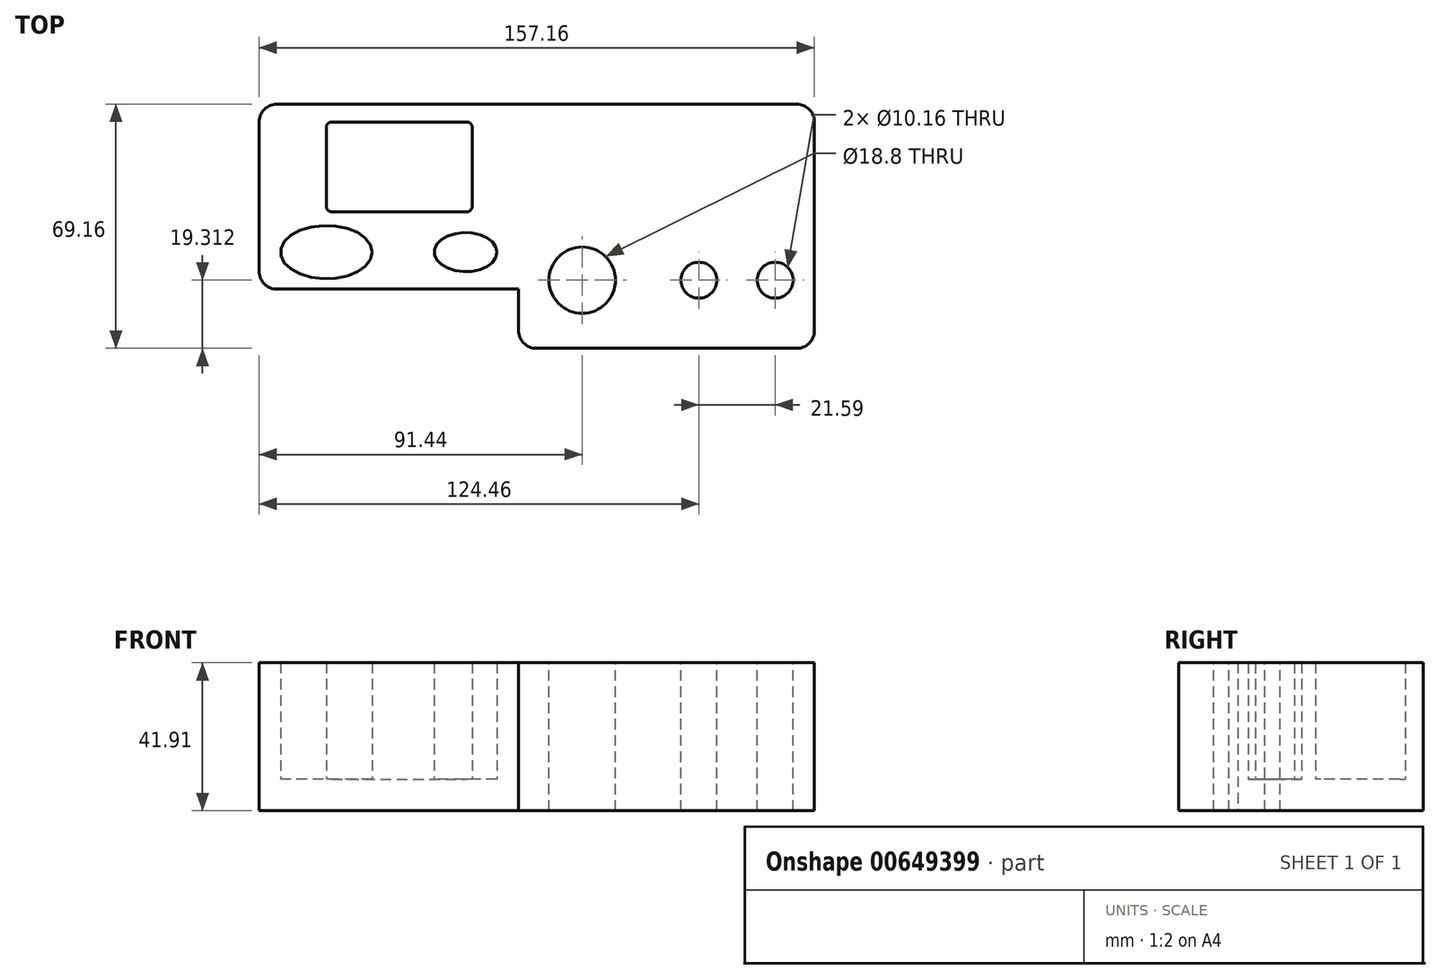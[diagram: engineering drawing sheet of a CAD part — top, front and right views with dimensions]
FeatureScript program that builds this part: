
annotation { "Feature Type Name" : "Feature", "Feature Type Description" : "" }
export const myFeature = defineFeature(function(context is Context, id is Id, definition is map)
    precondition{}
    {
        {
            var Q0;
            Q0=qCreatedBy(makeId("Top.planeOp"),FACE);
            var sketch = newSketch(context, id + "F0", { "sketchPlane" : qUnion([Q0])});
            skLineSegment(sketch, "E0.bottom", {"start": v(0, 0) * mm, "end": v(157.16, 0) * mm});
            skLineSegment(sketch, "E0.top", {"start": v(0, -52.39) * mm, "end": v(157.16, -52.39) * mm});
            skLineSegment(sketch, "E0.left", {"start": v(0, 0) * mm, "end": v(0, -52.39) * mm});
            skLineSegment(sketch, "E0.right", {"start": v(157.16, 0) * mm, "end": v(157.16, -52.39) * mm});
            skLineSegment(sketch, "E1.bottom", {"start": v(19.05, -5.08) * mm, "end": v(60.33, -5.08) * mm});
            skLineSegment(sketch, "E1.top", {"start": v(19.05, -30.48) * mm, "end": v(60.33, -30.48) * mm});
            skLineSegment(sketch, "E1.left", {"start": v(19.05, -5.08) * mm, "end": v(19.05, -30.48) * mm});
            skLineSegment(sketch, "E1.right", {"start": v(60.33, -5.08) * mm, "end": v(60.33, -30.48) * mm});
            skEllipse(sketch, "E2", {"center": v(58.42, -41.9) * mm, "majorRadius": 8.9 * mm, "minorRadius": 5.54 * mm, "majorAxis": v(1, 0)});
            skEllipse(sketch, "E3", {"center": v(19.05, -41.91) * mm, "majorRadius": 12.95 * mm, "minorRadius": 7.56 * mm, "majorAxis": v(1, 0)});
            skSolve(sketch);
        }
        {
            var Q0;
            Q0 = qSketchRegion(id + "F0", true);
            extrude(context, id + "F1", {"entities" : qUnion([Q0]), "depth" : 33.02 * mm, "offsetDistance" : 25.4 * mm});
        }
        {
            var Q0;
            Q0=qCreatedBy(makeId("Top.planeOp"),FACE);
            var sketch = newSketch(context, id + "F2", { "sketchPlane" : qUnion([Q0])});
            skLineSegment(sketch, "E4.bottom", {"start": v(0, 0) * mm, "end": v(73.03, 0) * mm});
            skLineSegment(sketch, "E4.top", {"start": v(0, -52.39) * mm, "end": v(73.03, -52.39) * mm});
            skLineSegment(sketch, "E4.left", {"start": v(0, 0) * mm, "end": v(0, -52.39) * mm});
            skLineSegment(sketch, "E4.right", {"start": v(73.03, 0) * mm, "end": v(73.03, -52.39) * mm});
            skSolve(sketch);
        }
        {
            var Q0;
            Q0 = qSketchRegion(id + "F2", true);
            extrude(context, id + "F3", {"entities" : qUnion([Q0]), "operationType" : NewBodyOperationType.ADD, "oppositeDirection" : true, "depth" : 8.9 * mm, "offsetDistance" : 25.4 * mm});
        }
        {
            var Q0;
            Q0=makeQuery(id+"F3.boolean.opBoolean","MERGE",EDGE,{"derivedFrom":[makeQuery(id+"F1.opExtrude","SWEPT_EDGE",EDGE,{"disambiguationData":[OSD([sQuery(id+"F0.wireOp",EDGE,"E0.top"),sQuery(id+"F0.wireOp",EDGE,"E0.right")])]}),makeQuery(id+"F3.opExtrude","SWEPT_EDGE",EDGE,{"disambiguationData":[OSD([sQuery(id+"F2.wireOp",EDGE,"E4.top"),sQuery(id+"F2.wireOp",EDGE,"E4.right")])]})]});
            var Q1;
            Q1=makeQuery(id+"F3.boolean.opBoolean","MERGE",EDGE,{"derivedFrom":[makeQuery(id+"F1.opExtrude","SWEPT_EDGE",EDGE,{"disambiguationData":[OSD([sQuery(id+"F0.wireOp",EDGE,"E0.bottom"),sQuery(id+"F0.wireOp",EDGE,"E0.right")])]}),makeQuery(id+"F3.opExtrude","SWEPT_EDGE",EDGE,{"disambiguationData":[OSD([sQuery(id+"F2.wireOp",EDGE,"E4.bottom"),sQuery(id+"F2.wireOp",EDGE,"E4.right")])]})]});
            var Q2;
            Q2=makeQuery(id+"F3.boolean.opBoolean","MERGE",EDGE,{"derivedFrom":[makeQuery(id+"F1.opExtrude","SWEPT_EDGE",EDGE,{"disambiguationData":[OSD([sQuery(id+"F0.wireOp",EDGE,"E0.bottom"),sQuery(id+"F0.wireOp",EDGE,"E0.left")])]}),makeQuery(id+"F3.opExtrude","SWEPT_EDGE",EDGE,{"disambiguationData":[OSD([sQuery(id+"F2.wireOp",EDGE,"E4.bottom"),sQuery(id+"F2.wireOp",EDGE,"E4.left")])]})]});
            var Q3;
            Q3=makeQuery(id+"F3.boolean.opBoolean","MERGE",EDGE,{"derivedFrom":[makeQuery(id+"F1.opExtrude","SWEPT_EDGE",EDGE,{"disambiguationData":[OSD([sQuery(id+"F0.wireOp",EDGE,"E0.top"),sQuery(id+"F0.wireOp",EDGE,"E0.left")])]}),makeQuery(id+"F3.opExtrude","SWEPT_EDGE",EDGE,{"disambiguationData":[OSD([sQuery(id+"F2.wireOp",EDGE,"E4.top"),sQuery(id+"F2.wireOp",EDGE,"E4.left")])]})]});
            fillet(context, id + "F4", {"entities" : qUnion([Q0, Q1, Q2, Q3]), "radius" : 5.08 * mm, "tangentPropagation" : true, "allowEdgeOverflow" : false});
        }
        {
            var Q0;
            Q0=makeQuery(id+"F1.opExtrude","SWEPT_EDGE",EDGE,{"disambiguationData":[OSD([sQuery(id+"F0.wireOp",EDGE,"E1.bottom"),sQuery(id+"F0.wireOp",EDGE,"E1.left")])]});
            var Q1;
            Q1=makeQuery(id+"F1.opExtrude","SWEPT_EDGE",EDGE,{"disambiguationData":[OSD([sQuery(id+"F0.wireOp",EDGE,"E1.top"),sQuery(id+"F0.wireOp",EDGE,"E1.left")])]});
            var Q2;
            Q2=makeQuery(id+"F1.opExtrude","SWEPT_EDGE",EDGE,{"disambiguationData":[OSD([sQuery(id+"F0.wireOp",EDGE,"E1.top"),sQuery(id+"F0.wireOp",EDGE,"E1.right")])]});
            var Q3;
            Q3=makeQuery(id+"F1.opExtrude","SWEPT_EDGE",EDGE,{"disambiguationData":[OSD([sQuery(id+"F0.wireOp",EDGE,"E1.bottom"),sQuery(id+"F0.wireOp",EDGE,"E1.right")])]});
            fillet(context, id + "F5", {"entities" : qUnion([Q0, Q1, Q2, Q3]), "radius" : 1.52 * mm, "tangentPropagation" : true, "allowEdgeOverflow" : false});
        }
        {
            var Q0;
            Q0=makeQuery(id+"F8.boolean.opBoolean","MERGE",FACE,{"derivedFrom":[makeQuery(id+"F1.opExtrude","CAP_FACE",FACE,{"disambiguationData":[OSD([sQuery(id+"F0.wireOp",EDGE,"E0.bottom"),sQuery(id+"F0.wireOp",EDGE,"E0.top"),sQuery(id+"F0.wireOp",EDGE,"E0.left"),sQuery(id+"F0.wireOp",EDGE,"E0.right"),sQuery(id+"F0.wireOp",EDGE,"E1.bottom"),sQuery(id+"F0.wireOp",EDGE,"E1.top"),sQuery(id+"F0.wireOp",EDGE,"E1.left"),sQuery(id+"F0.wireOp",EDGE,"E1.right"),sQuery(id+"F0.wireOp",EDGE,"E2"),sQuery(id+"F0.wireOp",EDGE,"E3")])],"isStart":true}),makeQuery(id+"F8.opExtrude","CAP_FACE",FACE,{"disambiguationData":[OSD([sQuery(id+"F7.wireOp",EDGE,"E5.bottom"),sQuery(id+"F7.wireOp",EDGE,"E5.top"),sQuery(id+"F7.wireOp",EDGE,"E5.left"),sQuery(id+"F7.wireOp",EDGE,"E5.right")])],"isStart":true})]});
            extrude(context, id + "F6", {"entities" : qUnion([Q0]), "operationType" : NewBodyOperationType.ADD, "depth" : 8.9 * mm, "offsetDistance" : 25.4 * mm});
        }
        {
            var Q0;
            Q0=qCreatedBy(makeId("Top.planeOp"),FACE);
            var sketch = newSketch(context, id + "F7", { "sketchPlane" : qUnion([Q0])});
            skLineSegment(sketch, "E5.bottom", {"start": v(157.16, 0) * mm, "end": v(73.41, 0) * mm});
            skLineSegment(sketch, "E5.top", {"start": v(157.16, -69.16) * mm, "end": v(73.41, -69.16) * mm});
            skLineSegment(sketch, "E5.left", {"start": v(157.16, 0) * mm, "end": v(157.16, -69.16) * mm});
            skLineSegment(sketch, "E5.right", {"start": v(73.41, 0) * mm, "end": v(73.41, -69.16) * mm});
            skSolve(sketch);
        }
        {
            var Q0;
            Q0=makeQuery(id+"F7.imprint","IMPRINT",FACE,{"disambiguationData":[TD([[makeQuery(id+"F7.imprint","IMPRINT",EDGE,{"derivedFrom":sQuery(id+"F7.wireOp",EDGE,"E5.bottom")}),1.0]])]});
            extrude(context, id + "F8", {"entities" : qUnion([Q0]), "operationType" : NewBodyOperationType.ADD, "depth" : 33.02 * mm, "offsetDistance" : 25.4 * mm});
        }
        {
            var Q0;
            Q0=makeQuery(id+"F8.opExtrude","CAP_FACE",FACE,{"disambiguationData":[OSD([sQuery(id+"F7.wireOp",EDGE,"E5.bottom"),sQuery(id+"F7.wireOp",EDGE,"E5.top"),sQuery(id+"F7.wireOp",EDGE,"E5.left"),sQuery(id+"F7.wireOp",EDGE,"E5.right")])],"isStart":true});
            extrude(context, id + "F9", {"entities" : qUnion([Q0]), "operationType" : NewBodyOperationType.ADD, "depth" : 8.9 * mm, "offsetDistance" : 25.4 * mm});
        }
        {
            var Q0;
            Q0=makeQuery(id+"F1.opExtrude","CAP_FACE",FACE,{"disambiguationData":[OSD([sQuery(id+"F0.wireOp",EDGE,"E0.bottom"),sQuery(id+"F0.wireOp",EDGE,"E0.top"),sQuery(id+"F0.wireOp",EDGE,"E0.left"),sQuery(id+"F0.wireOp",EDGE,"E0.right"),sQuery(id+"F0.wireOp",EDGE,"E1.bottom"),sQuery(id+"F0.wireOp",EDGE,"E1.top"),sQuery(id+"F0.wireOp",EDGE,"E1.left"),sQuery(id+"F0.wireOp",EDGE,"E1.right"),sQuery(id+"F0.wireOp",EDGE,"E2"),sQuery(id+"F0.wireOp",EDGE,"E3")])],"isStart":false});
            var sketch = newSketch(context, id + "F10", { "sketchPlane" : qUnion([Q0])});
            skCircle(sketch, "E6", {"center": v(91.44, -49.85) * mm, "radius": 9.4 * mm});
            skCircle(sketch, "E7", {"center": v(124.46, -49.85) * mm, "radius": 5.08 * mm});
            skCircle(sketch, "E8", {"center": v(146.05, -49.85) * mm, "radius": 5.08 * mm});
            skSolve(sketch);
        }
        {
            var Q0;
            Q0=makeQuery(id+"F10.imprint","IMPRINT",FACE,{"disambiguationData":[TD([[makeQuery(id+"F10.imprint","IMPRINT",EDGE,{"derivedFrom":sQuery(id+"F10.wireOp",EDGE,"E6")}),1.0]])]});
            var Q1;
            Q1=makeQuery(id+"F10.imprint","IMPRINT",FACE,{"disambiguationData":[TD([[makeQuery(id+"F10.imprint","IMPRINT",EDGE,{"derivedFrom":sQuery(id+"F10.wireOp",EDGE,"E7")}),1.0]])]});
            var Q2;
            Q2=makeQuery(id+"F10.imprint","IMPRINT",FACE,{"disambiguationData":[TD([[makeQuery(id+"F10.imprint","IMPRINT",EDGE,{"derivedFrom":sQuery(id+"F10.wireOp",EDGE,"E8")}),1.0]])]});
            extrude(context, id + "F11", {"entities" : qUnion([Q0, Q1, Q2]), "operationType" : NewBodyOperationType.REMOVE, "oppositeDirection" : true, "depth" : 50.8 * mm, "offsetDistance" : 25.4 * mm});
        }
        {
            var Q0;
            {var subQ0=sQuery(id+"F7.wireOp",EDGE,"E5.right");var subQ1=makeQuery(id+"F8.opExtrude","SWEPT_FACE",FACE,{"disambiguationData":[OSD([subQ0])]});var subQ2=sQuery(id+"F7.wireOp",EDGE,"E5.left");var subQ3=sQuery(id+"F7.wireOp",EDGE,"E5.top");var subQ4=sQuery(id+"F7.wireOp",EDGE,"E5.bottom");var subQ5=sQuery(id+"F0.wireOp",EDGE,"E0.top");var subQ6=sQuery(id+"F2.wireOp",EDGE,"E4.top");var subQ7=makeQuery(id+"F6.boolean.opBoolean","MERGE",FACE,{"derivedFrom":[makeQuery(id+"F3.boolean.opBoolean","MERGE",FACE,{"derivedFrom":[makeQuery(id+"F1.opExtrude","SWEPT_FACE",FACE,{"disambiguationData":[OSD([subQ5])]}),makeQuery(id+"F3.opExtrude","SWEPT_FACE",FACE,{"disambiguationData":[OSD([subQ6])]})]}),makeQuery(id+"F6.opExtrude","SWEPT_FACE",FACE,{"disambiguationData":[OSD([subQ5])]})]});Q0=makeQuery(id+"F9.boolean.opBoolean","MERGE",EDGE,{"derivedFrom":[makeQuery(id+"F8.boolean.opBoolean","INTERSECT",EDGE,{"derivedFrom":[subQ7,subQ1]}),makeQuery(id+"F9.opExtrude","SWEPT_EDGE",EDGE,{"disambiguationData":[OSD([subQ5,subQ6,subQ4,subQ3,subQ2,subQ0]),TDD([makeQuery(id+"F8.boolean.opBoolean","INTERSECT",VERTEX,{"derivedFrom":[subQ7,makeQuery(id+"F8.opExtrude","CAP_FACE",FACE,{"disambiguationData":[OSD([subQ4,subQ3,subQ2,subQ0])],"isStart":true}),subQ1]})])]})]});}
            var Q1;
            {var subQ0=sQuery(id+"F7.wireOp",EDGE,"E5.right");var subQ1=sQuery(id+"F7.wireOp",EDGE,"E5.top");Q1=makeQuery(id+"F9.boolean.opBoolean","MERGE",EDGE,{"derivedFrom":[makeQuery(id+"F8.opExtrude","SWEPT_EDGE",EDGE,{"disambiguationData":[OSD([subQ1,subQ0])]}),makeQuery(id+"F9.opExtrude","SWEPT_EDGE",EDGE,{"disambiguationData":[OSD([subQ1,subQ0])]})]});}
            var Q2;
            {var subQ0=sQuery(id+"F7.wireOp",EDGE,"E5.left");var subQ1=sQuery(id+"F7.wireOp",EDGE,"E5.top");Q2=makeQuery(id+"F9.boolean.opBoolean","MERGE",EDGE,{"derivedFrom":[makeQuery(id+"F8.opExtrude","SWEPT_EDGE",EDGE,{"disambiguationData":[OSD([subQ1,subQ0])]}),makeQuery(id+"F9.opExtrude","SWEPT_EDGE",EDGE,{"disambiguationData":[OSD([subQ1,subQ0])]})]});}
            var Q3;
            {var subQ0=sQuery(id+"F0.wireOp",EDGE,"E0.bottom");var subQ1=sQuery(id+"F0.wireOp",EDGE,"E0.right");Q3=makeQuery(id+"F8.boolean.opBoolean","SPLIT",EDGE,{"disambiguationData":[TD([makeQuery(id+"F8.opExtrude","CAP_FACE",FACE,{"disambiguationData":[OSD([sQuery(id+"F7.wireOp",EDGE,"E5.bottom"),sQuery(id+"F7.wireOp",EDGE,"E5.top"),sQuery(id+"F7.wireOp",EDGE,"E5.left"),sQuery(id+"F7.wireOp",EDGE,"E5.right")])],"isStart":false})])],"derivedFrom":makeQuery(id+"F6.boolean.opBoolean","MERGE",EDGE,{"derivedFrom":[makeQuery(id+"F1.opExtrude","SWEPT_EDGE",EDGE,{"disambiguationData":[OSD([subQ0,subQ1])]}),makeQuery(id+"F6.opExtrude","SWEPT_EDGE",EDGE,{"disambiguationData":[OSD([subQ0,subQ1])]})]})});}
            fillet(context, id + "F12", {"entities" : qUnion([Q0, Q1, Q2, Q3]), "tangentPropagation" : true, "radius" : 5.08 * mm, "defaultsChanged" : false, "vertexSettings" : [], "allowEdgeOverflow" : false});
        }
    });
